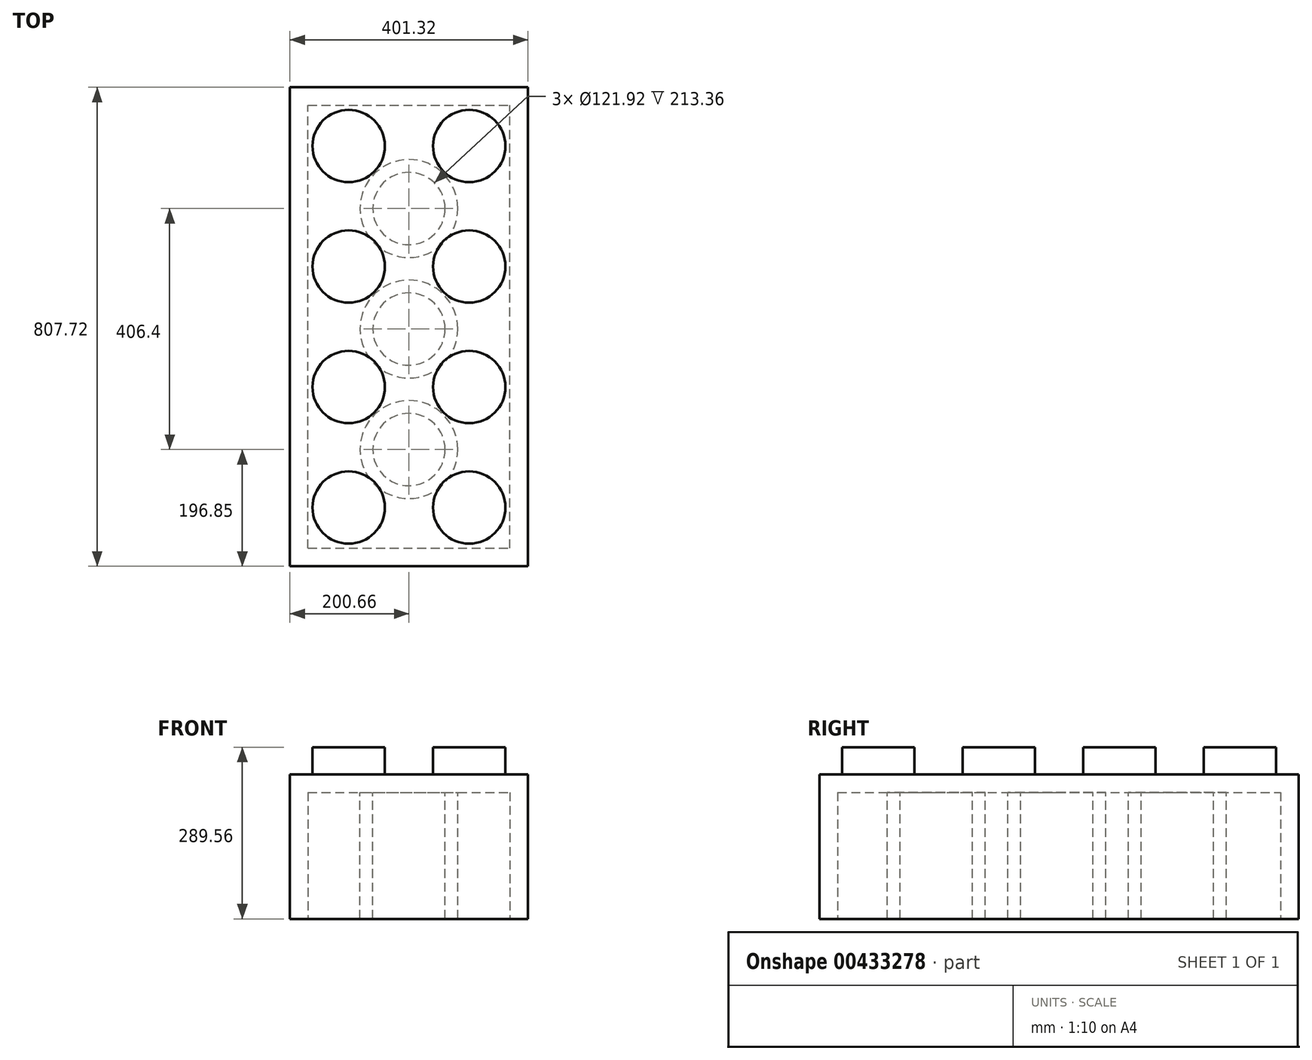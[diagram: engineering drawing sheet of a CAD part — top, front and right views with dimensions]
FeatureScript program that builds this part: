
annotation { "Feature Type Name" : "Feature", "Feature Type Description" : "" }
export const myFeature = defineFeature(function(context is Context, id is Id, definition is map)
    precondition{}
    {
        {
            var Q0;
            Q0=qCreatedBy(makeId("Front.planeOp"),FACE);
            var sketch = newSketch(context, id + "F0", { "sketchPlane" : qUnion([Q0])});
            skLineSegment(sketch, "E0.bottom", {"start": v(0, 152.08) * mm, "end": v(401.32, 152.08) * mm});
            skLineSegment(sketch, "E0.top", {"start": v(0, -91.76) * mm, "end": v(401.32, -91.76) * mm});
            skLineSegment(sketch, "E0.left", {"start": v(0, 152.08) * mm, "end": v(0, -91.76) * mm});
            skLineSegment(sketch, "E0.right", {"start": v(401.32, 152.08) * mm, "end": v(401.32, -91.76) * mm});
            skSolve(sketch);
        }
        {
            var Q0;
            Q0=makeQuery(id+"F0.imprint","IMPRINT",FACE,{"disambiguationData":[TD([[makeQuery(id+"F0.imprint","IMPRINT",EDGE,{"derivedFrom":sQuery(id+"F0.wireOp",EDGE,"E0.bottom")}),-1.0]])]});
            extrude(context, id + "F1", {"entities" : qUnion([Q0]), "oppositeDirection" : true, "depth" : 807.72 * mm});
        }
        {
            var Q0;
            Q0=makeQuery(id+"F1.opExtrude","SWEPT_FACE",FACE,{"disambiguationData":[OSD([sQuery(id+"F0.wireOp",EDGE,"E0.bottom")])]});
            var sketch = newSketch(context, id + "F2", { "sketchPlane" : qUnion([Q0])});
            skCircle(sketch, "E1", {"center": v(302.26, 99.06) * mm, "radius": 60.96 * mm});
            skCircle(sketch, "E2.0.1.0", {"center": v(302.26, 302.26) * mm, "radius": 60.96 * mm});
            skCircle(sketch, "E2.0.2.0", {"center": v(302.26, 505.46) * mm, "radius": 60.96 * mm});
            skCircle(sketch, "E2.0.3.0", {"center": v(302.26, 708.66) * mm, "radius": 60.96 * mm});
            skCircle(sketch, "E2.1.0.0", {"center": v(99.06, 99.06) * mm, "radius": 60.96 * mm});
            skCircle(sketch, "E2.1.1.0", {"center": v(99.06, 302.26) * mm, "radius": 60.96 * mm});
            skCircle(sketch, "E2.1.2.0", {"center": v(99.06, 505.46) * mm, "radius": 60.96 * mm});
            skCircle(sketch, "E2.1.3.0", {"center": v(99.06, 708.66) * mm, "radius": 60.96 * mm});
            skLineSegment(sketch, "E2.direction1", {"start": v(302.26, 99.06) * mm, "end": v(99.06, 99.06) * mm, "construction": true});
            skLineSegment(sketch, "E2.direction2", {"start": v(302.26, 99.06) * mm, "end": v(302.26, 302.26) * mm, "construction": true});
            skSolve(sketch);
        }
        {
            var Q0;
            Q0=makeQuery(id+"F2.imprint","IMPRINT",FACE,{"disambiguationData":[TD([[makeQuery(id+"F2.imprint","IMPRINT",EDGE,{"derivedFrom":sQuery(id+"F2.wireOp",EDGE,"E2.0.1.0")}),1.0]])]});
            var Q1;
            Q1=makeQuery(id+"F2.imprint","IMPRINT",FACE,{"disambiguationData":[TD([[makeQuery(id+"F2.imprint","IMPRINT",EDGE,{"derivedFrom":sQuery(id+"F2.wireOp",EDGE,"E1")}),1.0]])]});
            var Q2;
            Q2=makeQuery(id+"F2.imprint","IMPRINT",FACE,{"disambiguationData":[TD([[makeQuery(id+"F2.imprint","IMPRINT",EDGE,{"derivedFrom":sQuery(id+"F2.wireOp",EDGE,"E2.1.0.0")}),1.0]])]});
            var Q3;
            Q3=makeQuery(id+"F2.imprint","IMPRINT",FACE,{"disambiguationData":[TD([[makeQuery(id+"F2.imprint","IMPRINT",EDGE,{"derivedFrom":sQuery(id+"F2.wireOp",EDGE,"E2.1.1.0")}),1.0]])]});
            var Q4;
            Q4=makeQuery(id+"F2.imprint","IMPRINT",FACE,{"disambiguationData":[TD([[makeQuery(id+"F2.imprint","IMPRINT",EDGE,{"derivedFrom":sQuery(id+"F2.wireOp",EDGE,"E2.1.2.0")}),1.0]])]});
            var Q5;
            Q5=makeQuery(id+"F2.imprint","IMPRINT",FACE,{"disambiguationData":[TD([[makeQuery(id+"F2.imprint","IMPRINT",EDGE,{"derivedFrom":sQuery(id+"F2.wireOp",EDGE,"E2.0.2.0")}),1.0]])]});
            var Q6;
            Q6=makeQuery(id+"F2.imprint","IMPRINT",FACE,{"disambiguationData":[TD([[makeQuery(id+"F2.imprint","IMPRINT",EDGE,{"derivedFrom":sQuery(id+"F2.wireOp",EDGE,"E2.0.3.0")}),1.0]])]});
            var Q7;
            Q7=makeQuery(id+"F2.imprint","IMPRINT",FACE,{"disambiguationData":[TD([[makeQuery(id+"F2.imprint","IMPRINT",EDGE,{"derivedFrom":sQuery(id+"F2.wireOp",EDGE,"E2.1.3.0")}),1.0]])]});
            extrude(context, id + "F3", {"entities" : qUnion([Q0, Q1, Q2, Q3, Q4, Q5, Q6, Q7]), "operationType" : NewBodyOperationType.ADD, "depth" : 45.72 * mm});
        }
        {
            var Q0;
            Q0=makeQuery(id+"F1.opExtrude","SWEPT_FACE",FACE,{"disambiguationData":[OSD([sQuery(id+"F0.wireOp",EDGE,"E0.top")])]});
            var sketch = newSketch(context, id + "F4", { "sketchPlane" : qUnion([Q0])});
            skLineSegment(sketch, "E3.bottom", {"start": v(30.48, -30.48) * mm, "end": v(370.84, -30.48) * mm});
            skLineSegment(sketch, "E3.top", {"start": v(30.48, -777.24) * mm, "end": v(370.84, -777.24) * mm});
            skLineSegment(sketch, "E3.left", {"start": v(30.48, -30.48) * mm, "end": v(30.48, -777.24) * mm});
            skLineSegment(sketch, "E3.right", {"start": v(370.84, -30.48) * mm, "end": v(370.84, -777.24) * mm});
            skSolve(sketch);
        }
        {
            var Q0;
            Q0=makeQuery(id+"F4.imprint","IMPRINT",FACE,{"disambiguationData":[TD([[makeQuery(id+"F4.imprint","IMPRINT",EDGE,{"derivedFrom":sQuery(id+"F4.wireOp",EDGE,"E3.bottom")}),-1.0]])]});
            extrude(context, id + "F5", {"entities" : qUnion([Q0]), "operationType" : NewBodyOperationType.REMOVE, "oppositeDirection" : true, "depth" : 213.36 * mm});
        }
        {
            var Q0;
            Q0=makeQuery(id+"F5.boolean.opBoolean","COPY",FACE,{"derivedFrom":makeQuery(id+"F5.opExtrude","CAP_FACE",FACE,{"disambiguationData":[OSD([sQuery(id+"F4.wireOp",EDGE,"E3.bottom"),sQuery(id+"F4.wireOp",EDGE,"E3.top"),sQuery(id+"F4.wireOp",EDGE,"E3.left"),sQuery(id+"F4.wireOp",EDGE,"E3.right")])],"isStart":false})});
            var sketch = newSketch(context, id + "F6", { "sketchPlane" : qUnion([Q0])});
            skCircle(sketch, "E4", {"center": v(200.66, -196.85) * mm, "radius": 82.55 * mm});
            skCircle(sketch, "E5", {"center": v(200.66, -196.85) * mm, "radius": 60.96 * mm});
            skCircle(sketch, "E6.0.1.0", {"center": v(200.66, -400.05) * mm, "radius": 82.55 * mm});
            skCircle(sketch, "E6.0.1.1", {"center": v(200.66, -400.05) * mm, "radius": 60.96 * mm});
            skCircle(sketch, "E6.0.2.0", {"center": v(200.66, -603.25) * mm, "radius": 82.55 * mm});
            skCircle(sketch, "E6.0.2.1", {"center": v(200.66, -603.25) * mm, "radius": 60.96 * mm});
            skLineSegment(sketch, "E6.direction1", {"start": v(200.66, -196.85) * mm, "end": v(226.06, -196.85) * mm, "construction": true});
            skLineSegment(sketch, "E6.direction2", {"start": v(200.66, -196.85) * mm, "end": v(200.66, -400.05) * mm, "construction": true});
            skSolve(sketch);
        }
        {
            var Q0;
            Q0=makeQuery(id+"F6.imprint","IMPRINT",FACE,{"disambiguationData":[TD([[makeQuery(id+"F6.imprint","IMPRINT",EDGE,{"derivedFrom":sQuery(id+"F6.wireOp",EDGE,"E4")}),1.0]])]});
            var Q1;
            Q1=makeQuery(id+"F6.imprint","IMPRINT",FACE,{"disambiguationData":[TD([[makeQuery(id+"F6.imprint","IMPRINT",EDGE,{"derivedFrom":sQuery(id+"F6.wireOp",EDGE,"E6.0.2.0")}),1.0]])]});
            var Q2;
            Q2=makeQuery(id+"F6.imprint","IMPRINT",FACE,{"disambiguationData":[TD([[makeQuery(id+"F6.imprint","IMPRINT",EDGE,{"derivedFrom":sQuery(id+"F6.wireOp",EDGE,"E6.0.1.0")}),1.0]])]});
            extrude(context, id + "F7", {"entities" : qUnion([Q0, Q1, Q2]), "operationType" : NewBodyOperationType.ADD, "depth" : 213.36 * mm});
        }
    });
